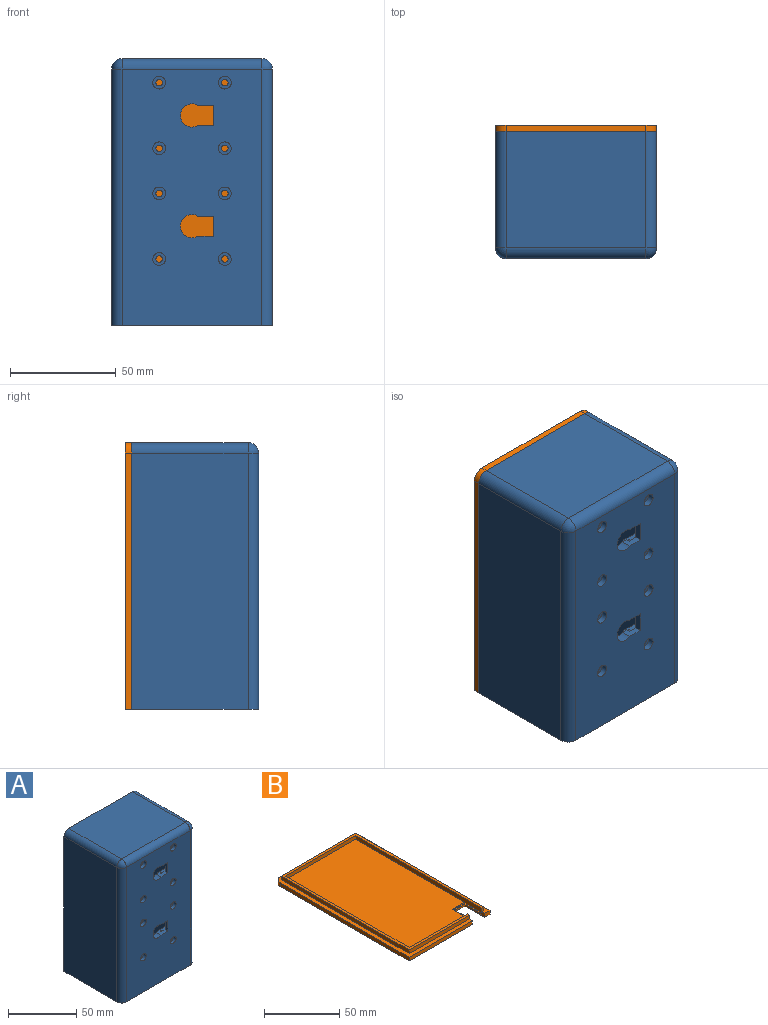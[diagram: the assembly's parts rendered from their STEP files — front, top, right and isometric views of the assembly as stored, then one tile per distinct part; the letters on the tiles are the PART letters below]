
ASSEMBLY  parts=2 mates=1
PART A: 87 faces, bbox 76x63x126 mm
  f0: plane 126x76mm, normal (0,1,0), area 1130.8mm2, adj f69,f70,f71,f72,f73,f74,f75,f76
  f1: plane 120x70mm, normal (0,1,0), area 4364.4mm2, adj f31,f32,f39,f40,f56,f57,f58,f59
  f2: plane 23x19.51mm, normal (0,1,0), area 231.7mm2, adj f4,f31,f32,f33,f35,f49,f51,f62
  f3: plane 23x19.51mm, normal (0,1,0), area 231.7mm2, adj f5,f38,f39,f40,f41,f53,f54,f55
  f4: cylinder r=5.5mm len=11mm, axis (0,-1,0), area 115.5mm2, adj f2,f6,f49,f51
  f5: cylinder r=5.5mm len=11mm, axis (0,-1,0), area 115.5mm2, adj f3,f6,f53,f54
  f6: plane 121x66mm, normal (0,-1,0), area 7469.1mm2, adj f4,f5,f9,f12,f15,f18,f21,f24
  f7: cylinder r=1.55mm len=6mm, axis (0,-1,0), area 58.4mm2, adj f8,f61
  f8: plane 6x6mm, normal (0,-1,0), area 20.7mm2, adj f7,f9
  f9: cylinder r=3mm len=6mm, axis (0,-1,0), area 56.5mm2, adj f6,f8
  f10: cylinder r=1.55mm len=6mm, axis (0,-1,0), area 58.4mm2, adj f11,f61
  f11: plane 6x6mm, normal (0,-1,0), area 20.7mm2, adj f10,f12
  f12: cylinder r=3mm len=6mm, axis (0,-1,0), area 56.5mm2, adj f6,f11
  f13: cylinder r=1.55mm len=6mm, axis (0,-1,0), area 58.4mm2, adj f14,f61
  f14: plane 6x6mm, normal (0,-1,0), area 20.7mm2, adj f13,f15
  f15: cylinder r=3mm len=6mm, axis (0,-1,0), area 56.5mm2, adj f6,f14
  f16: cylinder r=1.55mm len=6mm, axis (0,-1,0), area 58.4mm2, adj f17,f61
  f17: plane 6x6mm, normal (0,-1,0), area 20.7mm2, adj f16,f18
  f18: cylinder r=3mm len=6mm, axis (0,-1,0), area 56.5mm2, adj f6,f17
  f19: cylinder r=1.55mm len=6mm, axis (0,-1,0), area 58.4mm2, adj f20,f68
  f20: plane 6x6mm, normal (0,-1,0), area 20.7mm2, adj f19,f21
  f21: cylinder r=3mm len=6mm, axis (0,-1,0), area 56.5mm2, adj f6,f20
  f22: cylinder r=1.55mm len=6mm, axis (0,-1,0), area 58.4mm2, adj f23,f68
  f23: plane 6x6mm, normal (0,-1,0), area 20.7mm2, adj f22,f24
  f24: cylinder r=3mm len=6mm, axis (0,-1,0), area 56.5mm2, adj f6,f23
  f25: cylinder r=1.55mm len=6mm, axis (0,-1,0), area 58.4mm2, adj f26,f68
  f26: plane 6x6mm, normal (0,-1,0), area 20.7mm2, adj f25,f27
  f27: cylinder r=3mm len=6mm, axis (0,-1,0), area 56.5mm2, adj f6,f26
  f28: cylinder r=1.55mm len=6mm, axis (0,-1,0), area 58.4mm2, adj f29,f68
  f29: plane 6x6mm, normal (0,-1,0), area 20.7mm2, adj f28,f30
  f30: cylinder r=3mm len=6mm, axis (0,-1,0), area 56.5mm2, adj f6,f29
  f31: plane 29.5x6mm, normal (0,0,-1), area 111.6mm2, adj f1,f2,f35,f37,f62,f67,f68,f72
  f32: plane 29.5x6mm, normal (0,0,1), area 111.6mm2, adj f1,f2,f33,f37,f62,f63,f68,f72
  f33: plane 3.5x2mm, normal (1,0,0), area 7mm2, adj f2,f32,f37,f51
  f34: cylinder r=0.5mm len=2mm, axis (0,1,0), area 6.3mm2, adj f37,f46
  f35: plane 3.5x2mm, normal (1,0,0), area 7mm2, adj f2,f31,f37,f49
  f36: cylinder r=0.5mm len=2mm, axis (0,1,0), area 6.3mm2, adj f37,f45
  f37: plane 29.5x16.5mm, normal (0,1,0), area 442.4mm2, adj f31,f32,f33,f34,f35,f36,f49,f50
  f38: plane 3.5x2mm, normal (1,0,0), area 7mm2, adj f3,f39,f44,f54
  f39: plane 29.5x6mm, normal (0,0,-1), area 111.6mm2, adj f1,f3,f38,f44,f55,f60,f61,f72
  f40: plane 29.5x6mm, normal (0,0,1), area 111.6mm2, adj f1,f3,f41,f44,f55,f56,f61,f72
  f41: plane 3.5x2mm, normal (1,0,0), area 7mm2, adj f3,f40,f44,f53
  f42: cylinder r=0.5mm len=2mm, axis (0,1,0), area 6.3mm2, adj f44,f47
  f43: cylinder r=0.5mm len=2mm, axis (0,1,0), area 6.3mm2, adj f44,f48
  f44: plane 29.5x16.5mm, normal (0,1,0), area 442.4mm2, adj f38,f39,f40,f41,f42,f43,f52,f53
  f45: plane 1x1mm, normal (0,1,0), area 0.8mm2, adj f36
  f46: plane 1x1mm, normal (0,1,0), area 0.8mm2, adj f34
  f47: plane 1x1mm, normal (0,1,0), area 0.8mm2, adj f42
  f48: plane 1x1mm, normal (0,1,0), area 0.8mm2, adj f43
  f49: plane 7.23x5mm, normal (0,0,-1), area 27.1mm2, adj f2,f4,f6,f35,f37,f50
  f50: plane 9.5x3mm, normal (-1,0,0), area 28.5mm2, adj f6,f37,f49,f51
  f51: plane 7.23x5mm, normal (0,0,1), area 27.1mm2, adj f2,f4,f6,f33,f37,f50
  f52: plane 9.5x3mm, normal (-1,0,0), area 28.5mm2, adj f6,f44,f53,f54
  f53: plane 7.23x5mm, normal (0,0,1), area 27.1mm2, adj f3,f5,f6,f41,f44,f52
  f54: plane 7.23x5mm, normal (0,0,-1), area 27.1mm2, adj f3,f5,f6,f38,f44,f52
  f55: cylinder r=11.5mm len=23mm, axis (0,-1,0), area 215.4mm2, adj f3,f39,f40,f61
  f56: plane 12.9x4mm, normal (1,0,0), area 51.6mm2, adj f1,f40,f57,f61
  f57: plane 42.3x4mm, normal (0,0,-1), area 169.2mm2, adj f1,f56,f58,f61
  f58: plane 42.3x4mm, normal (-1,0,0), area 169.2mm2, adj f1,f57,f59,f61
  f59: plane 42.3x4mm, normal (0,0,1), area 169.2mm2, adj f1,f58,f60,f61
  f60: plane 12.9x4mm, normal (1,0,0), area 51.6mm2, adj f1,f39,f59,f61
  f61: plane 42.3x42.3mm, normal (0,1,0), area 1166.6mm2, adj f7,f10,f13,f16,f39,f40,f55,f56
  f62: cylinder r=11.5mm len=23mm, axis (0,-1,0), area 215.4mm2, adj f2,f31,f32,f68
  f63: plane 12.9x4mm, normal (1,0,0), area 51.6mm2, adj f1,f32,f64,f68
  f64: plane 42.3x4mm, normal (0,0,-1), area 169.2mm2, adj f1,f63,f65,f68
  f65: plane 42.3x4mm, normal (-1,0,0), area 169.2mm2, adj f1,f64,f66,f68
  f66: plane 42.3x4mm, normal (0,0,1), area 169.2mm2, adj f1,f65,f67,f68
  f67: plane 12.9x4mm, normal (1,0,0), area 51.6mm2, adj f1,f31,f66,f68
  f68: plane 42.3x42.3mm, normal (0,1,0), area 1166.6mm2, adj f19,f22,f25,f28,f31,f32,f62,f63
  f69: plane 70x58mm, normal (0,0,1), area 3884.5mm2, adj f0,f1,f71,f72,f84,f85,f86
  f70: plane 70x55mm, normal (0,0,-1), area 3850mm2, adj f0,f1,f71,f72
  f71: plane 120x55mm, normal (1,0,0), area 6600mm2, adj f0,f1,f69,f70
  f72: plane 120x57mm, normal (-1,0,0), area 6666mm2, adj f0,f1,f31,f32,f37,f39,f40,f44
  f73: plane 66x55mm, normal (0,0,1), area 3630mm2, adj f0,f77,f80,f83
  f74: plane 121x55mm, normal (-1,0,0), area 6655mm2, adj f0,f75,f81,f83
  f75: plane 76x63mm, normal (0,0,-1), area 4583.8mm2, adj f0,f6,f74,f76,f78,f81,f84,f85
  f76: plane 121x55mm, normal (1,0,0), area 6655mm2, adj f0,f75,f77,f78
  f77: cylinder r=5mm len=55mm, axis (0,-1,0), area 432mm2, adj f0,f73,f76,f79
  f78: cylinder r=5mm len=121mm, axis (0,0,1), area 950.3mm2, adj f6,f75,f76,f79
  f79: sphere r=5mm, area 39.3mm2, adj f77,f78,f80
  f80: cylinder r=5mm len=66mm, axis (-1,0,0), area 518.4mm2, adj f6,f73,f79,f82
  f81: cylinder r=5mm len=121mm, axis (0,0,-1), area 950.3mm2, adj f6,f74,f75,f82
  f82: sphere r=5mm, area 39.3mm2, adj f80,f81,f83
  f83: cylinder r=5mm len=55mm, axis (0,1,0), area 432mm2, adj f0,f73,f74,f82
  f84: plane 3x3mm, normal (-1,0,0), area 9mm2, adj f0,f69,f75,f86
  f85: plane 3x3mm, normal (1,0,0), area 9mm2, adj f0,f69,f75,f86
  f86: plane 11.5x3mm, normal (0,1,0), area 34.5mm2, adj f69,f75,f84,f85
PART B: 30 faces, bbox 76x126x6 mm
  f0: plane 15.5x11.5mm, normal (0,0,-1), area 40.5mm2, adj f2,f3,f9,f10,f13,f27,f28,f29
  f1: plane 15.5x11.5mm, normal (0,0,1), area 40.5mm2, adj f2,f3,f8,f10,f13,f27,f28,f29
  f2: plane 14.5x1.5mm, normal (-1,0,0), area 21.8mm2, adj f0,f1,f27,f29
  f3: plane 14.5x1.5mm, normal (1,0,0), area 21.7mm2, adj f0,f1,f27,f28
  f4: plane 54.5x3mm, normal (0,1,0), area 163.5mm2, adj f5,f10,f11,f24
  f5: plane 120x70mm, normal (0,0,1), area 721mm2, adj f4,f6,f10,f11,f12,f13,f14,f15
  f6: plane 56.5x3mm, normal (0,-1,0), area 169.5mm2, adj f5,f10,f15,f23
  f7: plane 5x3mm, normal (0,-1,0), area 15mm2, adj f13,f18,f22,f23
  f8: plane 11.5x0.75mm, normal (0,-1,0), area 8.6mm2, adj f1,f10,f13,f24
  f9: plane 11.5x0.75mm, normal (0,-1,0), area 8.6mm2, adj f0,f10,f13,f18
  f10: plane 18.5x6mm, normal (1,0,0), area 38.2mm2, adj f0,f1,f4,f5,f6,f8,f9,f18
  f11: plane 116x3mm, normal (1,0,0), area 348mm2, adj f4,f5,f12,f24
  f12: plane 66x3mm, normal (0,-1,0), area 198mm2, adj f5,f11,f13,f24
  f13: plane 121x6mm, normal (-1,0,0), area 386.2mm2, adj f0,f1,f5,f7,f8,f9,f12,f16
  f14: plane 70x3mm, normal (0,1,0), area 210mm2, adj f5,f15,f17,f23
  f15: plane 120x3mm, normal (-1,0,0), area 360mm2, adj f5,f6,f14,f23
  f16: plane 3x2mm, normal (0,-1,0), area 6mm2, adj f5,f13,f17,f23
  f17: plane 120x3mm, normal (1,0,0), area 360mm2, adj f5,f14,f16,f23
  f18: plane 126x76mm, normal (0,0,-1), area 9352.5mm2, adj f7,f9,f10,f13,f19,f20,f21,f22
  f19: plane 66x3mm, normal (0,1,0), area 198mm2, adj f18,f23,f25,f26
  f20: plane 121x3mm, normal (-1,0,0), area 363mm2, adj f18,f21,f23,f26
  f21: plane 59.5x3mm, normal (0,-1,0), area 178.5mm2, adj f10,f18,f20,f23
  f22: plane 121x3mm, normal (1,0,0), area 363mm2, adj f7,f18,f23,f25
  f23: plane 126x76mm, normal (0,0,1), area 1130.8mm2, adj f6,f7,f10,f13,f14,f15,f16,f17
  f24: plane 116x66mm, normal (0,0,1), area 7500.8mm2, adj f4,f8,f10,f11,f12,f13
  f25: cylinder r=5mm len=5mm, axis (0,0,-1), area 23.6mm2, adj f18,f19,f22,f23
  f26: cylinder r=5mm len=5mm, axis (0,0,-1), area 23.6mm2, adj f18,f19,f20,f23
  f27: plane 9.5x1.5mm, normal (0,-1,0), area 14.3mm2, adj f0,f1,f2,f3
  f28: plane 1.5x1mm, normal (0,-1,0), area 1.5mm2, adj f0,f1,f3,f10
  f29: plane 1.5x1mm, normal (0,-1,0), area 1.5mm2, adj f0,f1,f2,f13
PLACE A t=(-3,0,3)mm
PLACE B rot(axis=(1,0,0),90deg) t=(-3,63,3)mm
MATE fastened B.f23 <-> A.f0  axis (0,-1,0) through (-38,60,63)mm
